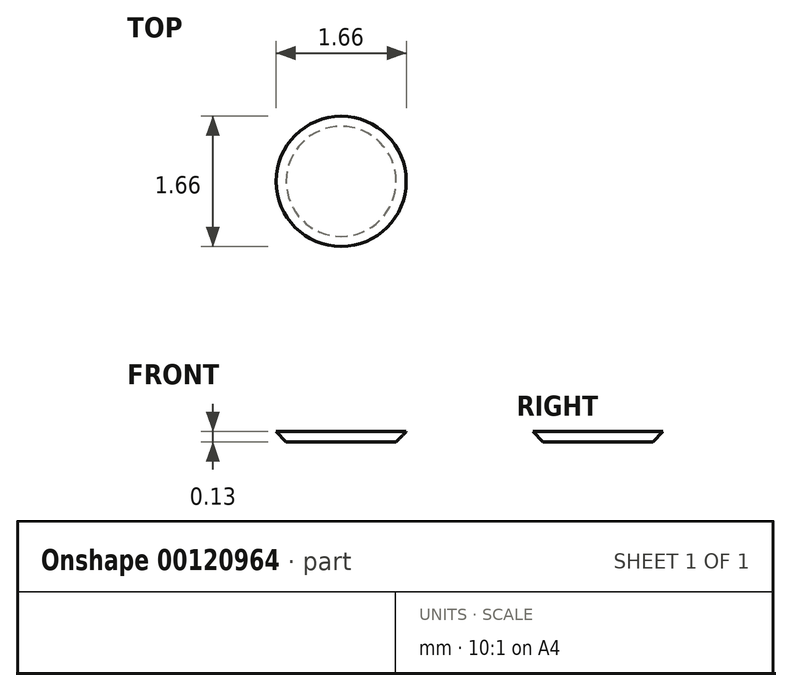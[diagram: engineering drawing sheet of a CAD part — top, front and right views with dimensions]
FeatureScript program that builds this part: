
annotation { "Feature Type Name" : "Feature", "Feature Type Description" : "" }
export const myFeature = defineFeature(function(context is Context, id is Id, definition is map)
    precondition{}
    {
        {
            var Q0;
            Q0=qCreatedBy(makeId("Top.planeOp"),FACE);
            var sketch = newSketch(context, id + "F0", { "sketchPlane" : qUnion([Q0])});
            skCircle(sketch, "E0", {"center": v(0, 0) * mm, "radius": 1.59 * mm});
            skSolve(sketch);
        }
        {
            var Q0;
            Q0=makeQuery(id+"F0.imprint","IMPRINT",FACE,{"disambiguationData":[TD([[makeQuery(id+"F0.imprint","IMPRINT",EDGE,{"derivedFrom":sQuery(id+"F0.wireOp",EDGE,"E0")}),1.0]])]});
            extrude(context, id + "F1", {"entities" : qUnion([Q0]), "oppositeDirection" : true, "depth" : 13 / 101.6 * mm});
        }
        {
            var Q0;
            Q0=makeQuery(id+"F1.opExtrude","CAP_EDGE",EDGE,{"disambiguationData":[OSD([sQuery(id+"F0.wireOp",EDGE,"E0")])],"isStart":false});
            chamfer(context, id + "F2", {"entities" : qUnion([Q0]), "width" : 0.89 * mm, "tangentPropagation" : true});
        }
    });
